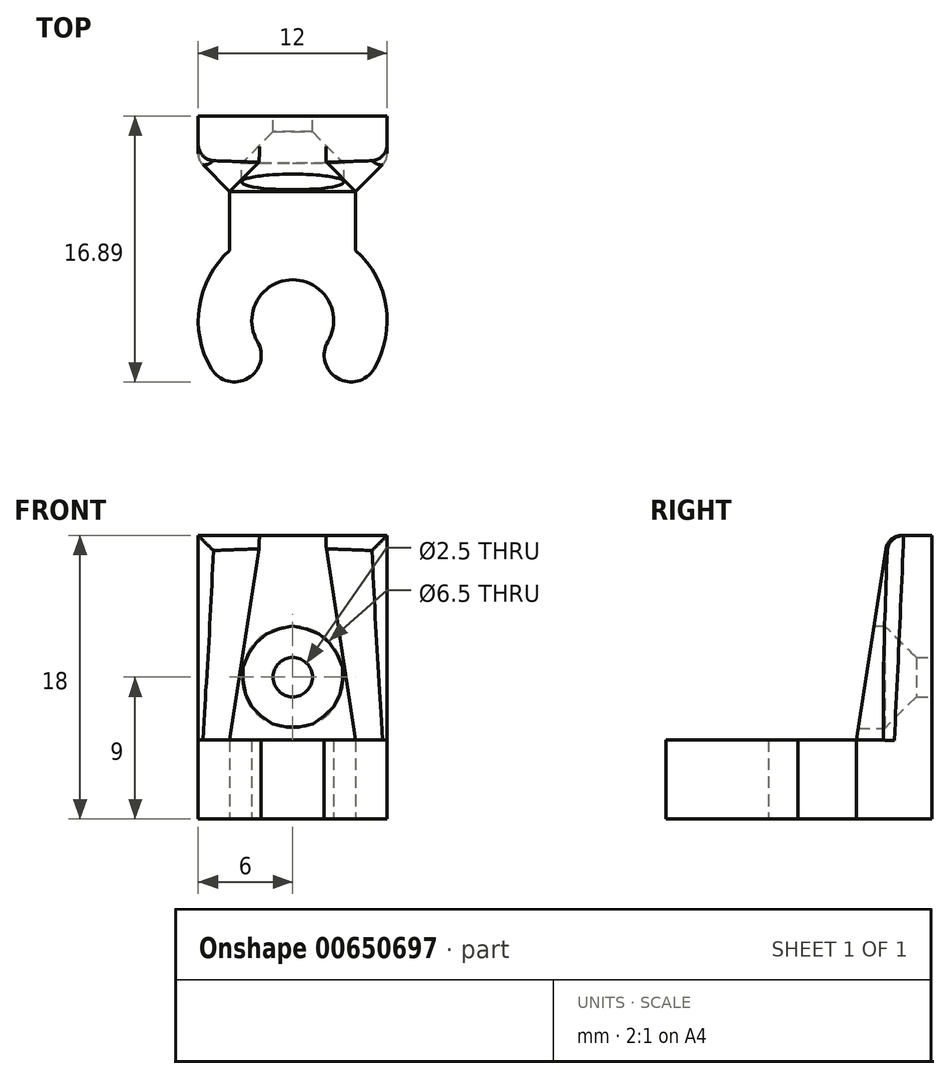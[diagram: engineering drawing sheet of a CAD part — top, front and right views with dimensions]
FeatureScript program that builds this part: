
annotation { "Feature Type Name" : "Feature", "Feature Type Description" : "" }
export const myFeature = defineFeature(function(context is Context, id is Id, definition is map)
    precondition{}
    {
        {
            var Q0;
            Q0=qCreatedBy(makeId("Top.planeOp"),FACE);
            var sketch = newSketch(context, id + "F0", { "sketchPlane" : qUnion([Q0])});
            skArc(sketch, "E0", {"start": v(5.16, -3.06) * mm, "mid": v(0, 6) * mm, "end": v(-5.16, -3.06) * mm});
            skLineSegment(sketch, "E1", {"start": v(-4, 4.47) * mm, "end": v(-4, 8.2) * mm});
            skLineSegment(sketch, "E2", {"start": v(-6, 10.2) * mm, "end": v(-6, 13) * mm});
            skLineSegment(sketch, "E3", {"start": v(-6, 13) * mm, "end": v(6, 13) * mm});
            skLineSegment(sketch, "E4", {"start": v(6, 13) * mm, "end": v(6, 10.2) * mm});
            skLineSegment(sketch, "E5", {"start": v(4, 8.2) * mm, "end": v(4, 4.47) * mm});
            skArc(sketch, "E6", {"start": v(2.24, -1.32) * mm, "mid": v(0, 2.6) * mm, "end": v(-2.24, -1.32) * mm});
            skArc(sketch, "E7", {"start": v(-5.16, -3.06) * mm, "mid": v(-2.83, -3.65) * mm, "end": v(-2.24, -1.32) * mm});
            skArc(sketch, "E8", {"start": v(2.24, -1.32) * mm, "mid": v(2.83, -3.65) * mm, "end": v(5.16, -3.06) * mm});
            skLineSegment(sketch, "E9", {"start": v(-4, 8.2) * mm, "end": v(-6, 10.2) * mm});
            skLineSegment(sketch, "E10", {"start": v(4, 8.2) * mm, "end": v(6, 10.2) * mm});
            skSolve(sketch);
        }
        {
            var Q0;
            Q0 = qSketchRegion(id + "F0", true);
            extrude(context, id + "F1", {"entities" : qUnion([Q0]), "depth" : 5 * mm, "offsetDistance" : 25 * mm});
        }
        {
            var Q0;
            Q0=qCreatedBy(makeId("Top.planeOp"),FACE);
            cPlane(context, id + "F2", {"entities" : qUnion([Q0]), "cplaneType" : CPlaneType.OFFSET, "offset" : 18 * mm, "width" : 150 * mm, "height" : 150 * mm});
        }
        {
            var Q0;
            Q0=qCreatedBy(id+"F2.planeOp",FACE);
            var sketch = newSketch(context, id + "F3", { "sketchPlane" : qUnion([Q0])});
            skLineSegment(sketch, "E11.0", {"start": v(6, 13) * mm, "end": v(6, 10.2) * mm});
            skLineSegment(sketch, "E11.1", {"start": v(-6, 13) * mm, "end": v(6, 13) * mm});
            skLineSegment(sketch, "E11.2", {"start": v(-6, 10.2) * mm, "end": v(-6, 13) * mm});
            skLineSegment(sketch, "E12", {"start": v(-6, 10.2) * mm, "end": v(6, 10.2) * mm});
            skSolve(sketch);
        }
        {
            var Q0;
            Q0=makeQuery(id+"F1.opExtrude","CAP_FACE",FACE,{"disambiguationData":[OSD([sQuery(id+"F0.wireOp",EDGE,"E0"),sQuery(id+"F0.wireOp",EDGE,"E1"),sQuery(id+"F0.wireOp",EDGE,"E2"),sQuery(id+"F0.wireOp",EDGE,"E3"),sQuery(id+"F0.wireOp",EDGE,"E4"),sQuery(id+"F0.wireOp",EDGE,"E5"),sQuery(id+"F0.wireOp",EDGE,"E6"),sQuery(id+"F0.wireOp",EDGE,"E7"),sQuery(id+"F0.wireOp",EDGE,"E8"),sQuery(id+"F0.wireOp",EDGE,"E9"),sQuery(id+"F0.wireOp",EDGE,"E10")])],"isStart":false});
            var sketch = newSketch(context, id + "F4", { "sketchPlane" : qUnion([Q0])});
            skLineSegment(sketch, "E13.0", {"start": v(-6, 10.2) * mm, "end": v(-6, 13) * mm});
            skLineSegment(sketch, "E13.1", {"start": v(-6, 13) * mm, "end": v(6, 13) * mm});
            skLineSegment(sketch, "E13.2", {"start": v(6, 13) * mm, "end": v(6, 10.2) * mm});
            skLineSegment(sketch, "E13.3", {"start": v(4, 8.2) * mm, "end": v(6, 10.2) * mm});
            skLineSegment(sketch, "E13.4", {"start": v(-4, 8.2) * mm, "end": v(-6, 10.2) * mm});
            skLineSegment(sketch, "E14", {"start": v(-4, 8.2) * mm, "end": v(4, 8.2) * mm});
            skSolve(sketch);
        }
        {
            var Q1;
            Q1 = qSketchRegion(id + "F3", true);
            var Q2;
            Q2 = qSketchRegion(id + "F4", true);
            var Q3;
            Q3=sQuery(id+"F4.wireOp",VERTEX,"E13.2.end");
            var Q4;
            Q4=sQuery(id+"F3.wireOp",VERTEX,"E11.0.end");
            loft(context, id + "F5", {"operationType" : NewBodyOperationType.ADD, "sheetProfilesArray" : [{ "sheetProfileEntities" : qUnion([Q1]) }, { "sheetProfileEntities" : qUnion([Q2]) }], "matchConnections" : true, "connections" : [{ "connectionEntities" : qUnion([Q3, Q4]), "connectionEdgeQueries" : qUnion([]), "connectionEdgeParameters" : [] }]});
        }
        {
            var Q0;
            Q0=makeQuery(id+"F5.boolean.opBoolean","MERGE",FACE,{"derivedFrom":[makeQuery(id+"F1.opExtrude","SWEPT_FACE",FACE,{"disambiguationData":[OSD([sQuery(id+"F0.wireOp",EDGE,"E3")])]}),makeQuery(id+"F5.opLoft","SWEPT_FACE",FACE,{"disambiguationData":[OSD([sQuery(id+"F3.wireOp",EDGE,"E11.0"),sQuery(id+"F3.wireOp",EDGE,"E11.1"),sQuery(id+"F3.wireOp",EDGE,"E11.2"),sQuery(id+"F4.wireOp",EDGE,"E13.0"),sQuery(id+"F4.wireOp",EDGE,"E13.1"),sQuery(id+"F4.wireOp",EDGE,"E13.2")])]})]});
            var sketch = newSketch(context, id + "F6", { "sketchPlane" : qUnion([Q0])});
            skCircle(sketch, "E15", {"center": v(0, 9) * mm, "radius": 1.25 * mm});
            skSolve(sketch);
        }
        {
            var Q0;
            Q0 = qSketchRegion(id + "F6", true);
            extrude(context, id + "F7", {"entities" : qUnion([Q0]), "operationType" : NewBodyOperationType.REMOVE, "oppositeDirection" : true, "depth" : 1 * mm, "offsetDistance" : 25 * mm});
        }
        {
            var Q0;
            Q0=makeQuery(id+"F7.boolean.opBoolean","COPY",FACE,{"derivedFrom":makeQuery(id+"F7.opExtrude","CAP_FACE",FACE,{"disambiguationData":[OSD([sQuery(id+"F6.wireOp",EDGE,"E15")])],"isStart":false})});
            var sketch = newSketch(context, id + "F8", { "sketchPlane" : qUnion([Q0])});
            skCircle(sketch, "E16.0", {"center": v(0, 9) * mm, "radius": 1.25 * mm});
            skSolve(sketch);
        }
        {
            var Q0;
            Q0 = qSketchRegion(id + "F8", true);
            extrude(context, id + "F9", {"entities" : qUnion([Q0]), "operationType" : NewBodyOperationType.REMOVE, "oppositeDirection" : true, "depth" : 2 * mm, "offsetDistance" : 25 * mm, "hasDraft" : true, "draftAngle" : 45 * degree});
        }
        {
            var Q0;
            Q0=makeQuery(id+"F9.boolean.opBoolean","COPY",FACE,{"derivedFrom":makeQuery(id+"F9.opExtrude","CAP_FACE",FACE,{"disambiguationData":[OSD([sQuery(id+"F8.wireOp",EDGE,"E16.0")])],"isStart":false})});
            var sketch = newSketch(context, id + "F10", { "sketchPlane" : qUnion([Q0])});
            skCircle(sketch, "E17.0", {"center": v(0, 9) * mm, "radius": 3.25 * mm});
            skSolve(sketch);
        }
        {
            var Q0;
            Q0 = qSketchRegion(id + "F10", true);
            extrude(context, id + "F11", {"entities" : qUnion([Q0]), "operationType" : NewBodyOperationType.REMOVE, "endBound" : BoundingType.UP_TO_NEXT, "oppositeDirection" : true, "depth" : 25 * mm, "offsetDistance" : 25 * mm});
        }
        {
            var Q0;
            Q0=makeQuery(id+"F5.opLoft","MID_CAP_EDGE",EDGE,{"disambiguationData":[OSD([sQuery(id+"F0.wireOp",EDGE,"E1"),sQuery(id+"F0.wireOp",EDGE,"E5"),sQuery(id+"F4.wireOp",EDGE,"E13.3"),sQuery(id+"F4.wireOp",EDGE,"E13.4"),sQuery(id+"F4.wireOp",EDGE,"E14")])],"capPos":1.0});
            var Q1;
            Q1=makeQuery(id+"F5.opLoft","SWEPT_EDGE",EDGE,{"disambiguationData":[OSD([sQuery(id+"F3.wireOp",EDGE,"E11.0"),sQuery(id+"F3.wireOp",EDGE,"E12"),sQuery(id+"F4.wireOp",EDGE,"E13.2"),sQuery(id+"F4.wireOp",EDGE,"E13.3")])]});
            var Q2;
            Q2=makeQuery(id+"F1.opExtrude","SWEPT_EDGE",EDGE,{"disambiguationData":[OSD([sQuery(id+"F0.wireOp",EDGE,"E4"),sQuery(id+"F0.wireOp",EDGE,"E10")])]});
            var Q3;
            Q3=makeQuery(id+"F5.opLoft","MID_CAP_EDGE",EDGE,{"disambiguationData":[OSD([sQuery(id+"F3.wireOp",EDGE,"E11.0"),sQuery(id+"F3.wireOp",EDGE,"E12"),sQuery(id+"F4.wireOp",EDGE,"E13.2"),sQuery(id+"F4.wireOp",EDGE,"E13.3")])],"capPos":0.0});
            var Q4;
            Q4=makeQuery(id+"F5.opLoft","MID_CAP_EDGE",EDGE,{"disambiguationData":[OSD([sQuery(id+"F0.wireOp",EDGE,"E5"),sQuery(id+"F3.wireOp",EDGE,"E12"),sQuery(id+"F4.wireOp",EDGE,"E13.2"),sQuery(id+"F4.wireOp",EDGE,"E13.3"),sQuery(id+"F4.wireOp",EDGE,"E14")])],"capPos":0.0});
            var Q5;
            Q5=makeQuery(id+"F5.opLoft","MID_CAP_EDGE",EDGE,{"disambiguationData":[OSD([sQuery(id+"F0.wireOp",EDGE,"E5"),sQuery(id+"F3.wireOp",EDGE,"E11.2"),sQuery(id+"F3.wireOp",EDGE,"E12"),sQuery(id+"F4.wireOp",EDGE,"E13.3"),sQuery(id+"F4.wireOp",EDGE,"E14")])],"capPos":0.0});
            var Q6;
            Q6=makeQuery(id+"F5.opLoft","SWEPT_EDGE",EDGE,{"disambiguationData":[OSD([sQuery(id+"F3.wireOp",EDGE,"E11.2"),sQuery(id+"F3.wireOp",EDGE,"E12"),sQuery(id+"F4.wireOp",EDGE,"E13.0"),sQuery(id+"F4.wireOp",EDGE,"E13.4")])]});
            var Q7;
            Q7=makeQuery(id+"F1.opExtrude","SWEPT_EDGE",EDGE,{"disambiguationData":[OSD([sQuery(id+"F0.wireOp",EDGE,"E2"),sQuery(id+"F0.wireOp",EDGE,"E9")])]});
            fillet(context, id + "F12", {"entities" : qUnion([Q0, Q1, Q2, Q3, Q4, Q5, Q6, Q7]), "radius" : 1 * mm, "tangentPropagation" : true, "allowEdgeOverflow" : false});
        }
    });
